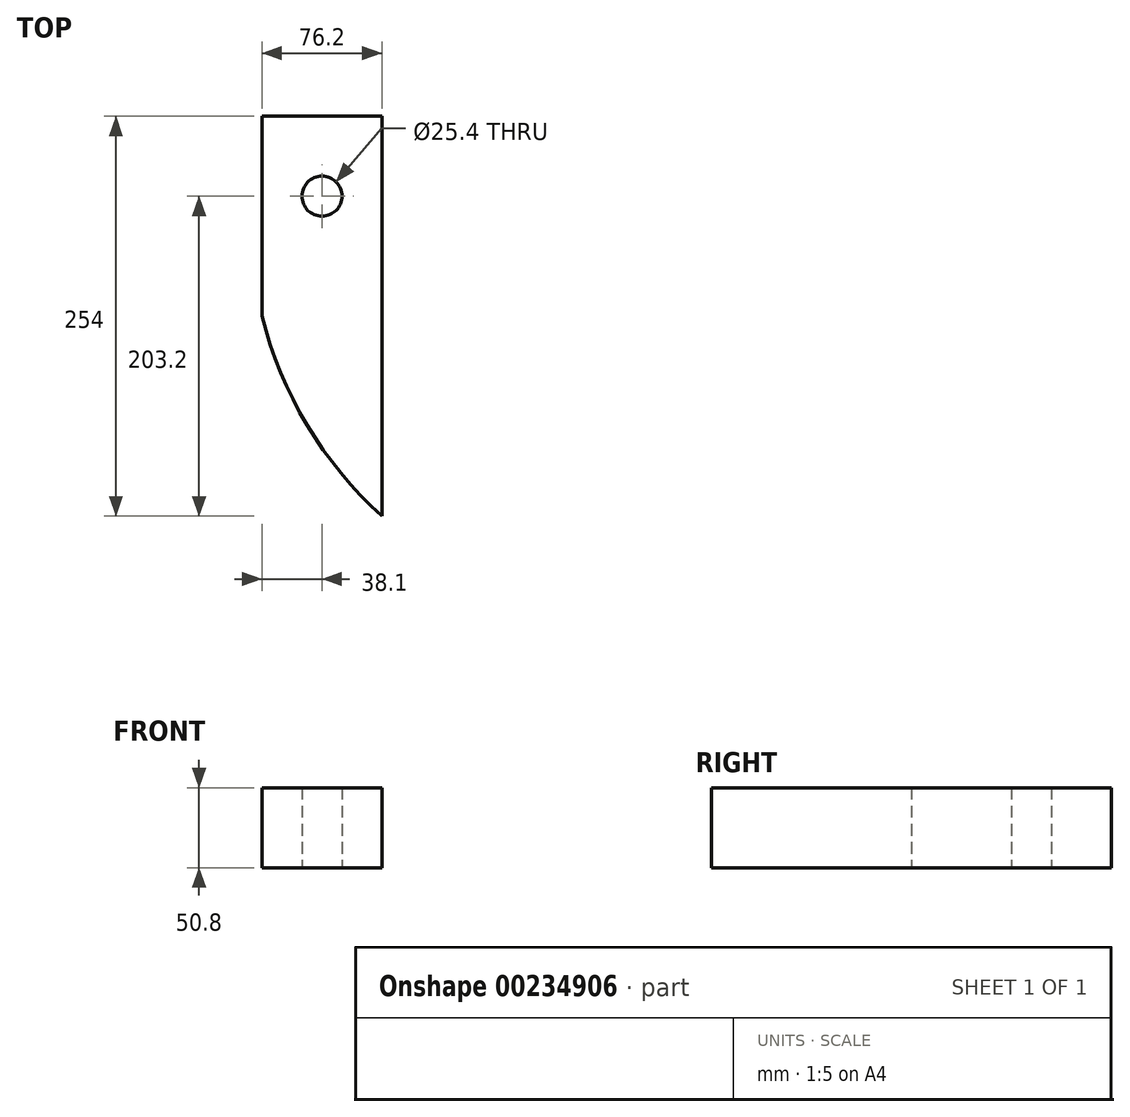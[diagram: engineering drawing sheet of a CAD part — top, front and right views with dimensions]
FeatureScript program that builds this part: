
annotation { "Feature Type Name" : "Feature", "Feature Type Description" : "" }
export const myFeature = defineFeature(function(context is Context, id is Id, definition is map)
    precondition{}
    {
        {
            var Q0;
            Q0=qCreatedBy(makeId("Top.planeOp"),FACE);
            var sketch = newSketch(context, id + "F0", { "sketchPlane" : qUnion([Q0])});
            skCircle(sketch, "E0", {"center": v(0, 0) * mm, "radius": 12.7 * mm});
            skLineSegment(sketch, "E1", {"start": v(-38.1, 50.8) * mm, "end": v(38.1, 50.8) * mm});
            skLineSegment(sketch, "E2", {"start": v(38.1, 50.8) * mm, "end": v(38.1, -203.2) * mm});
            skLineSegment(sketch, "E3", {"start": v(-38.1, 50.8) * mm, "end": v(-38.1, -76.2) * mm});
            skArc(sketch, "E4", {"start": v(-38.1, -76.2) * mm, "mid": v(-9.46, -145.38) * mm, "end": v(38.1, -203.2) * mm});
            skLineSegment(sketch, "E5", {"start": v(0, 50.8) * mm, "end": v(0, 0) * mm, "construction": true});
            skPoint(sketch, "E5.startSnap0", {"position": v(0, 50.8) * mm});
            skSolve(sketch);
        }
        {
            var Q0;
            Q0=makeQuery(id+"F0.imprint","IMPRINT",FACE,{"disambiguationData":[TD([[makeQuery(id+"F0.imprint","IMPRINT",EDGE,{"derivedFrom":sQuery(id+"F0.wireOp",EDGE,"E0")}),-1.0]])]});
            extrude(context, id + "F1", {"entities" : qUnion([Q0]), "depth" : 50.8 * mm});
        }
    });
